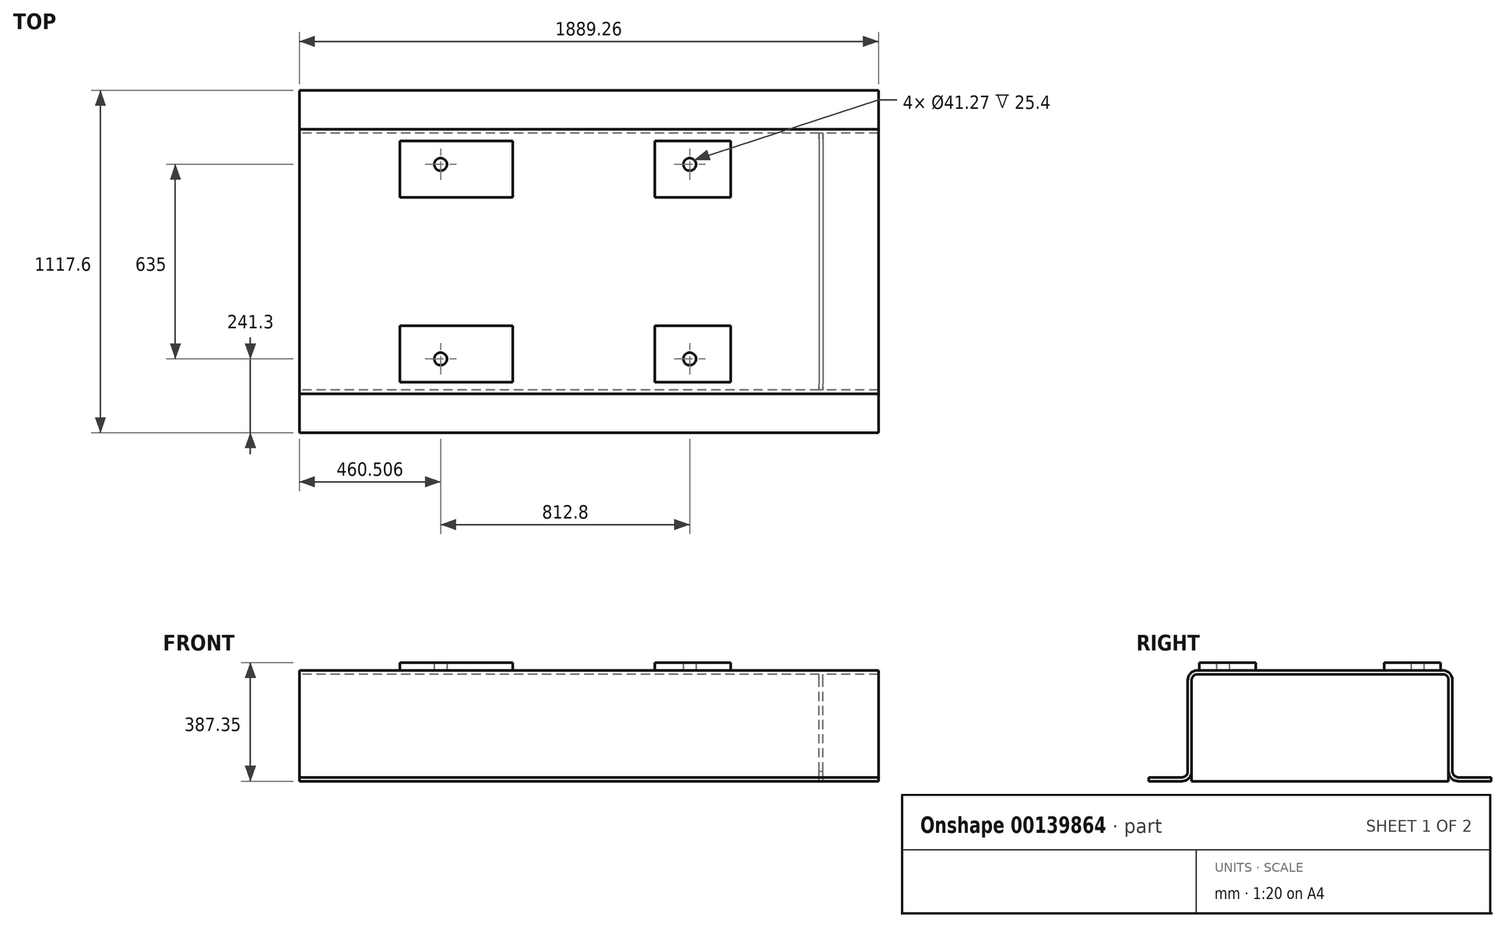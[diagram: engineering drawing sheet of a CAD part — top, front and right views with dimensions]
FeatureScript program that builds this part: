
annotation { "Feature Type Name" : "Feature", "Feature Type Description" : "" }
export const myFeature = defineFeature(function(context is Context, id is Id, definition is map)
    precondition{}
    {
        {
            var Q0;
            Q0=qCreatedBy(makeId("Right.planeOp"),FACE);
            var sketch = newSketch(context, id + "F0", { "sketchPlane" : qUnion([Q0])});
            skLineSegment(sketch, "E0", {"start": v(-558.8, 0) * mm, "end": v(558.8, 0) * mm, "construction": true});
            skLineSegment(sketch, "E1.0", {"start": v(-558.8, 361.95) * mm, "end": v(558.8, 361.95) * mm, "construction": true});
            skLineSegment(sketch, "E2.bottom", {"start": v(0, 361.95) * mm, "end": v(400.05, 361.95) * mm});
            skLineSegment(sketch, "E2.top", {"start": v(450.85, 0) * mm, "end": v(558.8, 0) * mm});
            skLineSegment(sketch, "E2.right", {"start": v(558.8, 12.7) * mm, "end": v(558.8, 0) * mm});
            skLineSegment(sketch, "E3.0", {"start": v(0, 349.25) * mm, "end": v(400.05, 349.25) * mm});
            skLineSegment(sketch, "E4.0", {"start": v(450.85, 12.7) * mm, "end": v(558.8, 12.7) * mm});
            skLineSegment(sketch, "E5", {"start": v(0, -75.24) * mm, "end": v(0, 457.7) * mm, "construction": true});
            skLineSegment(sketch, "E6.0", {"start": v(431.8, 31.75) * mm, "end": v(431.8, 330.2) * mm});
            skLineSegment(sketch, "E7.0", {"start": v(419.1, 31.75) * mm, "end": v(419.1, 330.2) * mm});
            skArc(sketch, "E8.filletArc", {"start": v(419.1, 330.2) * mm, "mid": v(413.52, 343.67) * mm, "end": v(400.05, 349.25) * mm});
            skArc(sketch, "E9.filletArc", {"start": v(431.8, 31.75) * mm, "mid": v(437.38, 18.28) * mm, "end": v(450.85, 12.7) * mm});
            skArc(sketch, "E10.filletArc", {"start": v(431.8, 330.2) * mm, "mid": v(422.5, 352.65) * mm, "end": v(400.05, 361.95) * mm});
            skArc(sketch, "E11.filletArc", {"start": v(419.1, 31.75) * mm, "mid": v(428.4, 9.3) * mm, "end": v(450.85, 0) * mm});
            skLineSegment(sketch, "E12.0", {"start": v(450.85, 6.35) * mm, "end": v(558.8, 6.35) * mm});
            skArc(sketch, "E13.MirrorCS", {"start": v(-419.1, 330.2) * mm, "mid": v(-413.52, 343.67) * mm, "end": v(-400.05, 349.25) * mm});
            skLineSegment(sketch, "E14.MirrorCS", {"start": v(-558.8, 12.7) * mm, "end": v(-558.8, 0) * mm});
            skArc(sketch, "E15.MirrorCS", {"start": v(-431.8, 31.75) * mm, "mid": v(-437.38, 18.28) * mm, "end": v(-450.85, 12.7) * mm});
            skLineSegment(sketch, "E16.MirrorCS", {"start": v(-450.85, 6.35) * mm, "end": v(-558.8, 6.35) * mm});
            skLineSegment(sketch, "E17.MirrorCS", {"start": v(-450.85, 12.7) * mm, "end": v(-558.8, 12.7) * mm});
            skLineSegment(sketch, "E18.MirrorCS", {"start": v(-450.85, 0) * mm, "end": v(-558.8, 0) * mm});
            skArc(sketch, "E19.MirrorCS", {"start": v(-419.1, 31.75) * mm, "mid": v(-428.4, 9.3) * mm, "end": v(-450.85, 0) * mm});
            skArc(sketch, "E20.MirrorCS", {"start": v(-431.8, 330.2) * mm, "mid": v(-422.5, 352.65) * mm, "end": v(-400.05, 361.95) * mm});
            skLineSegment(sketch, "E21.MirrorCS", {"start": v(-431.8, 31.75) * mm, "end": v(-431.8, 330.2) * mm});
            skLineSegment(sketch, "E22.MirrorCS", {"start": v(0, 349.25) * mm, "end": v(-400.05, 349.25) * mm});
            skLineSegment(sketch, "E23.MirrorCS", {"start": v(-419.1, 31.75) * mm, "end": v(-419.1, 330.2) * mm});
            skLineSegment(sketch, "E24.MirrorCS", {"start": v(0, 361.95) * mm, "end": v(-400.05, 361.95) * mm});
            skSolve(sketch);
        }
        {
            var Q0;
            Q0=qSketchRegion(id+"F0",true);
            extrude(context, id + "F1", {"entities" : qUnion([Q0]), "endBound" : BoundingType.SYMMETRIC, "depth" : 1889.25 * mm});
        }
        {
            var Q0;
            Q0=makeQuery(id+"F1.opExtrude","SWEPT_FACE",FACE,{"disambiguationData":[OSD([sQuery(id+"F0.wireOp",EDGE,"E3.0"),sQuery(id+"F0.wireOp",EDGE,"E22.MirrorCS")])]});
            var sketch = newSketch(context, id + "F2", { "sketchPlane" : qUnion([Q0])});
            skLineSegment(sketch, "E25.0", {"start": v(763.78, 419.1) * mm, "end": v(751.08, 419.1) * mm});
            skLineSegment(sketch, "E26.0", {"start": v(763.78, -419.1) * mm, "end": v(751.08, -419.1) * mm});
            skLineSegment(sketch, "E27.0", {"start": v(763.78, -419.1) * mm, "end": v(763.78, 419.1) * mm});
            skLineSegment(sketch, "E28.0", {"start": v(751.08, -419.1) * mm, "end": v(751.08, 419.1) * mm});
            skPoint(sketch, "E29.orphan", {"position": v(-944.63, 419.1) * mm});
            skPoint(sketch, "E30.orphan", {"position": v(944.63, 419.1) * mm});
            skPoint(sketch, "E31.orphan", {"position": v(944.63, -419.1) * mm});
            skPoint(sketch, "E32.orphan", {"position": v(-944.63, -419.1) * mm});
            skSolve(sketch);
        }
        {
            var Q0;
            Q0=qSketchRegion(id+"F2",true);
            var Q1;
            Q1=makeQuery(id+"F1.opExtrude","SWEPT_FACE",FACE,{"disambiguationData":[OSD([sQuery(id+"F0.wireOp",EDGE,"E18.MirrorCS")])]});
            extrude(context, id + "F3", {"entities" : qUnion([Q0]), "operationType" : NewBodyOperationType.ADD, "endBound" : BoundingType.UP_TO_SURFACE, "endBoundEntityFace" : qUnion([Q1]), "depth" : 25.4 * mm});
        }
        {
            var Q0;
            Q0=makeQuery(id+"F1.opExtrude","SWEPT_FACE",FACE,{"disambiguationData":[OSD([sQuery(id+"F0.wireOp",EDGE,"E2.bottom"),sQuery(id+"F0.wireOp",EDGE,"E24.MirrorCS")])]});
            var sketch = newSketch(context, id + "F4", { "sketchPlane" : qUnion([Q0])});
            skLineSegment(sketch, "E33.0", {"start": v(-1820.93, -1308.8) * mm, "end": v(-1820.93, -495.23) * mm, "construction": true});
            skLineSegment(sketch, "E34.0", {"start": v(-1319.28, -1308.8) * mm, "end": v(-1319.28, -495.23) * mm, "construction": true});
            skLineSegment(sketch, "E35.0", {"start": v(-77.72, -1308.8) * mm, "end": v(-77.72, 594.77) * mm, "construction": true});
            skLineSegment(sketch, "E36.0", {"start": v(716.03, -1308.8) * mm, "end": v(716.03, -495.23) * mm, "construction": true});
            skLineSegment(sketch, "E37.0", {"start": v(-249.17, -1308.8) * mm, "end": v(-249.17, 594.77) * mm, "construction": true});
            skLineSegment(sketch, "E38.0", {"start": v(-617.47, -1308.8) * mm, "end": v(-617.47, 594.77) * mm, "construction": true});
            skLineSegment(sketch, "E39.0", {"start": v(214.38, -1308.8) * mm, "end": v(214.38, 594.77) * mm, "construction": true});
            skLineSegment(sketch, "E40.0", {"start": v(462.03, -1308.8) * mm, "end": v(462.03, 594.77) * mm, "construction": true});
            skLineSegment(sketch, "E41", {"start": v(-1320.83, 0) * mm, "end": v(1097.9, 0) * mm, "construction": true});
            skLineSegment(sketch, "E42.0", {"start": v(-1320.83, 209.55) * mm, "end": v(1097.9, 209.55) * mm, "construction": true});
            skLineSegment(sketch, "E43.0", {"start": v(-1320.83, 393.7) * mm, "end": v(1097.9, 393.7) * mm, "construction": true});
            skLineSegment(sketch, "E44.bottom", {"start": v(-617.47, 393.7) * mm, "end": v(-249.17, 393.7) * mm});
            skLineSegment(sketch, "E44.top", {"start": v(-617.47, 209.55) * mm, "end": v(-249.17, 209.55) * mm});
            skLineSegment(sketch, "E44.left", {"start": v(-617.47, 393.7) * mm, "end": v(-617.47, 209.55) * mm});
            skLineSegment(sketch, "E44.right", {"start": v(-249.17, 393.7) * mm, "end": v(-249.17, 209.55) * mm});
            skLineSegment(sketch, "E45.bottom", {"start": v(214.38, 209.55) * mm, "end": v(462.03, 209.55) * mm});
            skLineSegment(sketch, "E45.top", {"start": v(214.38, 393.7) * mm, "end": v(462.03, 393.7) * mm});
            skLineSegment(sketch, "E45.left", {"start": v(214.38, 209.55) * mm, "end": v(214.38, 393.7) * mm});
            skLineSegment(sketch, "E45.right", {"start": v(462.03, 209.55) * mm, "end": v(462.03, 393.7) * mm});
            skLineSegment(sketch, "E46.0", {"start": v(-484.12, -1308.8) * mm, "end": v(-484.12, 594.77) * mm, "construction": true});
            skLineSegment(sketch, "E47.0", {"start": v(328.68, -1308.8) * mm, "end": v(328.68, 594.77) * mm, "construction": true});
            skLineSegment(sketch, "E48.0", {"start": v(-1320.83, 317.5) * mm, "end": v(1097.9, 317.5) * mm, "construction": true});
            skCircle(sketch, "E49", {"center": v(-484.12, 317.5) * mm, "radius": 20.64 * mm});
            skCircle(sketch, "E50", {"center": v(328.68, 317.5) * mm, "radius": 20.64 * mm});
            skCircle(sketch, "E51.MirrorC", {"center": v(-484.12, -317.5) * mm, "radius": 20.64 * mm});
            skCircle(sketch, "E52.MirrorC", {"center": v(328.68, -317.5) * mm, "radius": 20.64 * mm});
            skLineSegment(sketch, "E53.MirrorCS", {"start": v(214.38, -393.7) * mm, "end": v(462.03, -393.7) * mm});
            skLineSegment(sketch, "E54.MirrorCS", {"start": v(214.38, -209.55) * mm, "end": v(214.38, -393.7) * mm});
            skLineSegment(sketch, "E55.MirrorCS", {"start": v(462.03, -209.55) * mm, "end": v(462.03, -393.7) * mm});
            skLineSegment(sketch, "E56.MirrorCS", {"start": v(-617.47, -393.7) * mm, "end": v(-617.47, -209.55) * mm});
            skLineSegment(sketch, "E57.MirrorCS", {"start": v(-617.47, -393.7) * mm, "end": v(-249.17, -393.7) * mm});
            skLineSegment(sketch, "E58.MirrorCS", {"start": v(-617.47, -209.55) * mm, "end": v(-249.17, -209.55) * mm});
            skLineSegment(sketch, "E59.MirrorCS", {"start": v(214.38, -209.55) * mm, "end": v(462.03, -209.55) * mm});
            skLineSegment(sketch, "E60.MirrorCS", {"start": v(-249.17, -393.7) * mm, "end": v(-249.17, -209.55) * mm});
            skSolve(sketch);
        }
        {
            var Q0;
            Q0=qSketchRegion(id+"F4",true);
            extrude(context, id + "F5", {"entities" : qUnion([Q0]), "operationType" : NewBodyOperationType.ADD, "depth" : 25.4 * mm});
        }
    });
